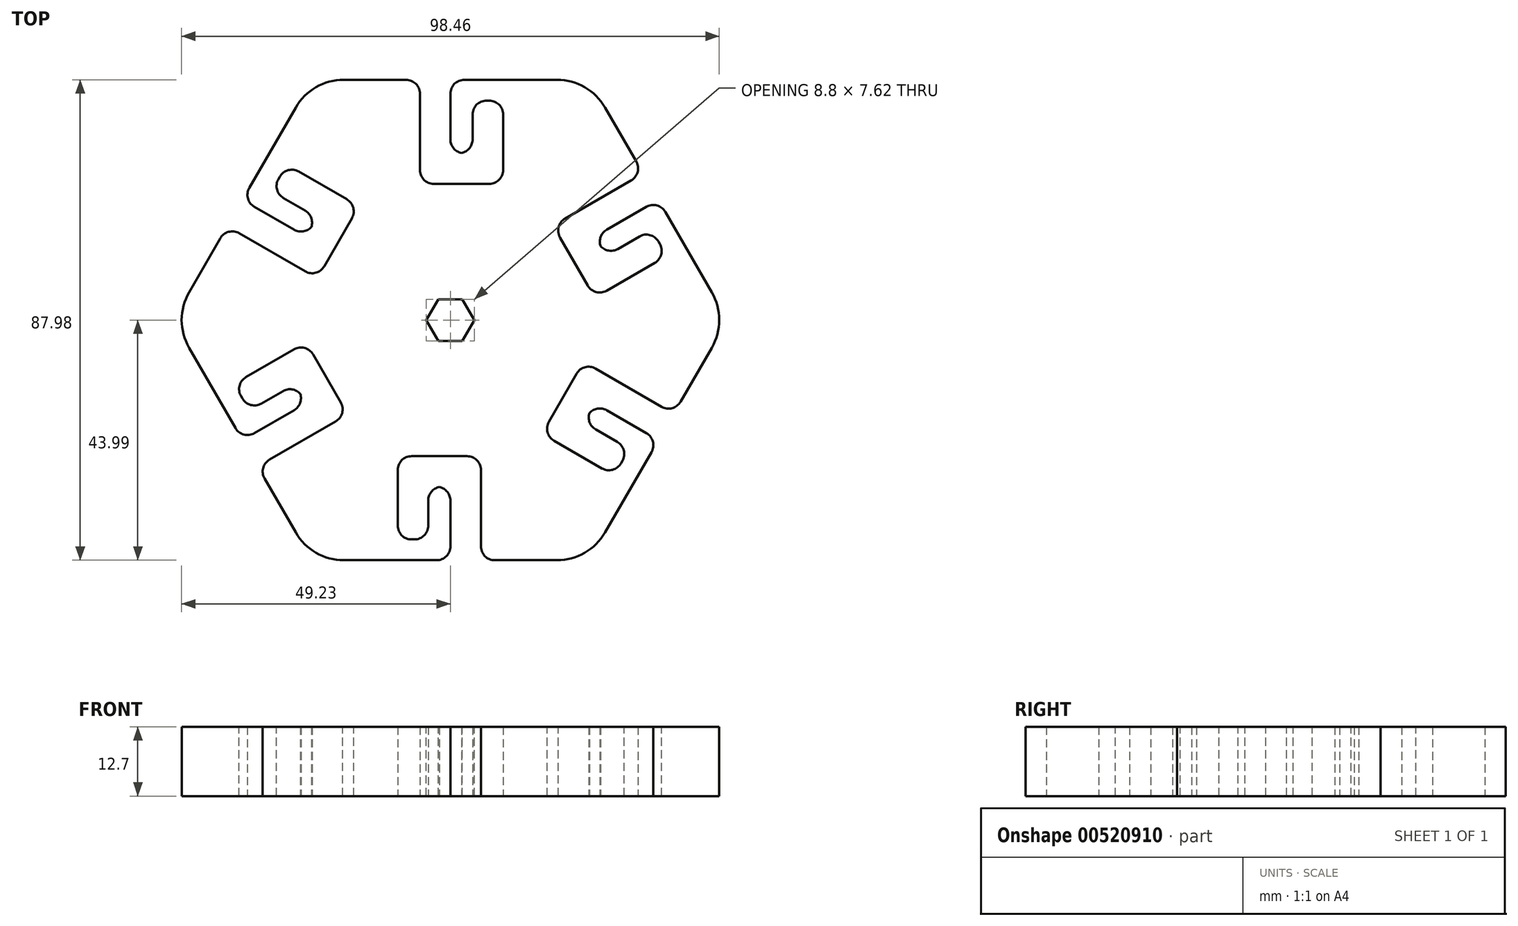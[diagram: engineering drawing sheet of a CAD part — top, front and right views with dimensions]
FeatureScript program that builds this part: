
annotation { "Feature Type Name" : "Feature", "Feature Type Description" : "" }
export const myFeature = defineFeature(function(context is Context, id is Id, definition is map)
    precondition{}
    {
        {
            var Q0;
            Q0=qCreatedBy(makeId("Top.planeOp"),FACE);
            var sketch = newSketch(context, id + "F0", { "sketchPlane" : qUnion([Q0])});
            skLineSegment(sketch, "E0", {"start": v(-5.59, 44) * mm, "end": v(-5.59, 24.94) * mm});
            skLineSegment(sketch, "E1", {"start": v(-5.59, 24.94) * mm, "end": v(9.65, 24.94) * mm});
            skLineSegment(sketch, "E2", {"start": v(9.65, 24.94) * mm, "end": v(9.65, 40.18) * mm});
            skLineSegment(sketch, "E3", {"start": v(9.65, 40.18) * mm, "end": v(4.06, 40.18) * mm});
            skLineSegment(sketch, "E4", {"start": v(4.06, 40.18) * mm, "end": v(4.06, 30.53) * mm});
            skLineSegment(sketch, "E5", {"start": v(4.06, 30.53) * mm, "end": v(0, 30.53) * mm});
            skLineSegment(sketch, "E6", {"start": v(0, 30.53) * mm, "end": v(0, 44) * mm});
            skCircle(sketch, "E7.cCircle", {"center": v(0, 0) * mm, "radius": 50.8 * mm, "construction": true});
            skLineSegment(sketch, "E7.0", {"start": v(25.4, -44) * mm, "end": v(-25.4, -44) * mm});
            skLineSegment(sketch, "E7.1", {"start": v(-25.4, -44) * mm, "end": v(-50.8, 0) * mm});
            skLineSegment(sketch, "E7.2", {"start": v(-50.8, 0) * mm, "end": v(-25.4, 44) * mm});
            skLineSegment(sketch, "E7.3", {"start": v(-25.4, 44) * mm, "end": v(25.4, 44) * mm});
            skLineSegment(sketch, "E7.4", {"start": v(25.4, 44) * mm, "end": v(50.8, 0) * mm});
            skLineSegment(sketch, "E7.5", {"start": v(50.8, 0) * mm, "end": v(25.4, -44) * mm});
            skLineSegment(sketch, "E8.1.0", {"start": v(-16.78, 20.83) * mm, "end": v(-29.97, 28.45) * mm});
            skLineSegment(sketch, "E8.1.1", {"start": v(-24.4, 7.63) * mm, "end": v(-16.78, 20.83) * mm});
            skLineSegment(sketch, "E8.1.2", {"start": v(-40.9, 17.16) * mm, "end": v(-24.4, 7.63) * mm});
            skLineSegment(sketch, "E8.1.3", {"start": v(-26.44, 15.27) * mm, "end": v(-38.1, 22) * mm});
            skLineSegment(sketch, "E8.1.4", {"start": v(-24.4, 18.79) * mm, "end": v(-26.44, 15.27) * mm});
            skLineSegment(sketch, "E8.1.5", {"start": v(-32.77, 23.61) * mm, "end": v(-24.4, 18.79) * mm});
            skLineSegment(sketch, "E8.1.6", {"start": v(-29.97, 28.45) * mm, "end": v(-32.77, 23.61) * mm});
            skLineSegment(sketch, "E8.2.0", {"start": v(-26.43, -4.11) * mm, "end": v(-39.63, -11.73) * mm});
            skLineSegment(sketch, "E8.2.1", {"start": v(-18.8, -17.31) * mm, "end": v(-26.43, -4.11) * mm});
            skLineSegment(sketch, "E8.2.2", {"start": v(-35.3, -26.84) * mm, "end": v(-18.8, -17.31) * mm});
            skLineSegment(sketch, "E8.2.3", {"start": v(-26.44, -15.27) * mm, "end": v(-38.1, -22) * mm});
            skLineSegment(sketch, "E8.2.4", {"start": v(-28.47, -11.75) * mm, "end": v(-26.44, -15.27) * mm});
            skLineSegment(sketch, "E8.2.5", {"start": v(-36.83, -16.57) * mm, "end": v(-28.47, -11.75) * mm});
            skLineSegment(sketch, "E8.2.6", {"start": v(-39.63, -11.73) * mm, "end": v(-36.83, -16.57) * mm});
            skLineSegment(sketch, "E8.3.0", {"start": v(-9.65, -24.94) * mm, "end": v(-9.65, -40.18) * mm});
            skLineSegment(sketch, "E8.3.1", {"start": v(5.59, -24.94) * mm, "end": v(-9.65, -24.94) * mm});
            skLineSegment(sketch, "E8.3.2", {"start": v(5.59, -44) * mm, "end": v(5.59, -24.94) * mm});
            skLineSegment(sketch, "E8.3.3", {"start": v(0, -30.53) * mm, "end": v(0, -44) * mm});
            skLineSegment(sketch, "E8.3.4", {"start": v(-4.06, -30.53) * mm, "end": v(0, -30.53) * mm});
            skLineSegment(sketch, "E8.3.5", {"start": v(-4.06, -40.18) * mm, "end": v(-4.06, -30.53) * mm});
            skLineSegment(sketch, "E8.3.6", {"start": v(-9.65, -40.18) * mm, "end": v(-4.06, -40.18) * mm});
            skLineSegment(sketch, "E8.4.0", {"start": v(16.78, -20.83) * mm, "end": v(29.97, -28.45) * mm});
            skLineSegment(sketch, "E8.4.1", {"start": v(24.4, -7.63) * mm, "end": v(16.78, -20.83) * mm});
            skLineSegment(sketch, "E8.4.2", {"start": v(40.9, -17.16) * mm, "end": v(24.4, -7.63) * mm});
            skLineSegment(sketch, "E8.4.3", {"start": v(26.44, -15.27) * mm, "end": v(38.1, -22) * mm});
            skLineSegment(sketch, "E8.4.4", {"start": v(24.4, -18.79) * mm, "end": v(26.44, -15.27) * mm});
            skLineSegment(sketch, "E8.4.5", {"start": v(32.77, -23.61) * mm, "end": v(24.4, -18.79) * mm});
            skLineSegment(sketch, "E8.4.6", {"start": v(29.97, -28.45) * mm, "end": v(32.77, -23.61) * mm});
            skLineSegment(sketch, "E8.5.0", {"start": v(26.43, 4.11) * mm, "end": v(39.63, 11.73) * mm});
            skLineSegment(sketch, "E8.5.1", {"start": v(18.8, 17.31) * mm, "end": v(26.43, 4.11) * mm});
            skLineSegment(sketch, "E8.5.2", {"start": v(35.3, 26.84) * mm, "end": v(18.8, 17.31) * mm});
            skLineSegment(sketch, "E8.5.3", {"start": v(26.44, 15.27) * mm, "end": v(38.1, 22) * mm});
            skLineSegment(sketch, "E8.5.4", {"start": v(28.47, 11.75) * mm, "end": v(26.44, 15.27) * mm});
            skLineSegment(sketch, "E8.5.5", {"start": v(36.83, 16.57) * mm, "end": v(28.47, 11.75) * mm});
            skLineSegment(sketch, "E8.5.6", {"start": v(39.63, 11.73) * mm, "end": v(36.83, 16.57) * mm});
            skPoint(sketch, "E9", {"position": v(2.03, 30.53) * mm});
            skSolve(sketch);
        }
        {
            var Q0;
            {var subQ12=sQuery(id+"F0.wireOp",EDGE,"E0");Q0=makeQuery(id+"F0.imprint","IMPRINT",FACE,{"disambiguationData":[TD([[makeQuery(id+"F0.imprint","IMPRINT",EDGE,{"derivedFrom":subQ12}),-1.0]])]});}
            extrude(context, id + "F1", {"entities" : qUnion([Q0]), "depth" : 12.7 * mm, "offsetDistance" : 25.4 * mm});
        }
        {
            var Q0;
            Q0=makeQuery(id+"F1.opExtrude","SWEPT_EDGE",EDGE,{"disambiguationData":[OSD([sQuery(id+"F0.wireOp",EDGE,"E7.1"),sQuery(id+"F0.wireOp",EDGE,"E7.2")])]});
            var Q1;
            Q1=makeQuery(id+"F1.opExtrude","SWEPT_EDGE",EDGE,{"disambiguationData":[OSD([sQuery(id+"F0.wireOp",EDGE,"E7.0"),sQuery(id+"F0.wireOp",EDGE,"E7.1")])]});
            var Q2;
            Q2=makeQuery(id+"F1.opExtrude","SWEPT_EDGE",EDGE,{"disambiguationData":[OSD([sQuery(id+"F0.wireOp",EDGE,"E7.0"),sQuery(id+"F0.wireOp",EDGE,"E7.5")])]});
            var Q3;
            Q3=makeQuery(id+"F1.opExtrude","SWEPT_EDGE",EDGE,{"disambiguationData":[OSD([sQuery(id+"F0.wireOp",EDGE,"E7.4"),sQuery(id+"F0.wireOp",EDGE,"E7.5")])]});
            var Q4;
            Q4=makeQuery(id+"F1.opExtrude","SWEPT_EDGE",EDGE,{"disambiguationData":[OSD([sQuery(id+"F0.wireOp",EDGE,"E7.3"),sQuery(id+"F0.wireOp",EDGE,"E7.4")])]});
            var Q5;
            Q5=makeQuery(id+"F1.opExtrude","SWEPT_EDGE",EDGE,{"disambiguationData":[OSD([sQuery(id+"F0.wireOp",EDGE,"E7.2"),sQuery(id+"F0.wireOp",EDGE,"E7.3")])]});
            fillet(context, id + "F2", {"entities" : qUnion([Q0, Q1, Q2, Q3, Q4, Q5]), "radius" : 10.16 * mm, "tangentPropagation" : true, "allowEdgeOverflow" : false});
        }
        {
            var Q0;
            Q0=makeQuery(id+"F1.opExtrude","SWEPT_EDGE",EDGE,{"disambiguationData":[OSD([sQuery(id+"F0.wireOp",EDGE,"E7.4"),sQuery(id+"F0.wireOp",EDGE,"E8.5.2")])]});
            var Q1;
            Q1=makeQuery(id+"F1.opExtrude","SWEPT_EDGE",EDGE,{"disambiguationData":[OSD([sQuery(id+"F0.wireOp",EDGE,"E8.5.1"),sQuery(id+"F0.wireOp",EDGE,"E8.5.2")])]});
            var Q2;
            Q2=makeQuery(id+"F1.opExtrude","SWEPT_EDGE",EDGE,{"disambiguationData":[OSD([sQuery(id+"F0.wireOp",EDGE,"E8.5.0"),sQuery(id+"F0.wireOp",EDGE,"E8.5.1")])]});
            var Q3;
            Q3=makeQuery(id+"F1.opExtrude","SWEPT_EDGE",EDGE,{"disambiguationData":[OSD([sQuery(id+"F0.wireOp",EDGE,"E8.5.0"),sQuery(id+"F0.wireOp",EDGE,"E8.5.6")])]});
            var Q4;
            Q4=makeQuery(id+"F1.opExtrude","SWEPT_EDGE",EDGE,{"disambiguationData":[OSD([sQuery(id+"F0.wireOp",EDGE,"E8.5.5"),sQuery(id+"F0.wireOp",EDGE,"E8.5.6")])]});
            var Q5;
            Q5=makeQuery(id+"F1.opExtrude","SWEPT_EDGE",EDGE,{"disambiguationData":[OSD([sQuery(id+"F0.wireOp",EDGE,"E8.5.4"),sQuery(id+"F0.wireOp",EDGE,"E8.5.5")])]});
            var Q6;
            Q6=makeQuery(id+"F1.opExtrude","SWEPT_EDGE",EDGE,{"disambiguationData":[OSD([sQuery(id+"F0.wireOp",EDGE,"E8.5.3"),sQuery(id+"F0.wireOp",EDGE,"E8.5.4")])]});
            var Q7;
            Q7=makeQuery(id+"F1.opExtrude","SWEPT_EDGE",EDGE,{"disambiguationData":[OSD([sQuery(id+"F0.wireOp",EDGE,"E7.4"),sQuery(id+"F0.wireOp",EDGE,"E8.5.3")])]});
            var Q8;
            Q8=makeQuery(id+"F1.opExtrude","SWEPT_EDGE",EDGE,{"disambiguationData":[OSD([sQuery(id+"F0.wireOp",EDGE,"E7.5"),sQuery(id+"F0.wireOp",EDGE,"E8.4.2")])]});
            var Q9;
            Q9=makeQuery(id+"F1.opExtrude","SWEPT_EDGE",EDGE,{"disambiguationData":[OSD([sQuery(id+"F0.wireOp",EDGE,"E7.5"),sQuery(id+"F0.wireOp",EDGE,"E8.4.3")])]});
            var Q10;
            Q10=makeQuery(id+"F1.opExtrude","SWEPT_EDGE",EDGE,{"disambiguationData":[OSD([sQuery(id+"F0.wireOp",EDGE,"E8.4.3"),sQuery(id+"F0.wireOp",EDGE,"E8.4.4")])]});
            var Q11;
            Q11=makeQuery(id+"F1.opExtrude","SWEPT_EDGE",EDGE,{"disambiguationData":[OSD([sQuery(id+"F0.wireOp",EDGE,"E8.4.1"),sQuery(id+"F0.wireOp",EDGE,"E8.4.2")])]});
            var Q12;
            Q12=makeQuery(id+"F1.opExtrude","SWEPT_EDGE",EDGE,{"disambiguationData":[OSD([sQuery(id+"F0.wireOp",EDGE,"E8.4.0"),sQuery(id+"F0.wireOp",EDGE,"E8.4.1")])]});
            var Q13;
            Q13=makeQuery(id+"F1.opExtrude","SWEPT_EDGE",EDGE,{"disambiguationData":[OSD([sQuery(id+"F0.wireOp",EDGE,"E8.4.0"),sQuery(id+"F0.wireOp",EDGE,"E8.4.6")])]});
            var Q14;
            Q14=makeQuery(id+"F1.opExtrude","SWEPT_EDGE",EDGE,{"disambiguationData":[OSD([sQuery(id+"F0.wireOp",EDGE,"E8.4.4"),sQuery(id+"F0.wireOp",EDGE,"E8.4.5")])]});
            var Q15;
            Q15=makeQuery(id+"F1.opExtrude","SWEPT_EDGE",EDGE,{"disambiguationData":[OSD([sQuery(id+"F0.wireOp",EDGE,"E8.4.5"),sQuery(id+"F0.wireOp",EDGE,"E8.4.6")])]});
            var Q16;
            Q16=makeQuery(id+"F1.opExtrude","SWEPT_EDGE",EDGE,{"disambiguationData":[OSD([sQuery(id+"F0.wireOp",EDGE,"E7.0"),sQuery(id+"F0.wireOp",EDGE,"E8.3.2")])]});
            var Q17;
            Q17=makeQuery(id+"F1.opExtrude","SWEPT_EDGE",EDGE,{"disambiguationData":[OSD([sQuery(id+"F0.wireOp",EDGE,"E7.0"),sQuery(id+"F0.wireOp",EDGE,"E8.3.3")])]});
            var Q18;
            Q18=makeQuery(id+"F1.opExtrude","SWEPT_EDGE",EDGE,{"disambiguationData":[OSD([sQuery(id+"F0.wireOp",EDGE,"E8.3.1"),sQuery(id+"F0.wireOp",EDGE,"E8.3.2")])]});
            var Q19;
            Q19=makeQuery(id+"F1.opExtrude","SWEPT_EDGE",EDGE,{"disambiguationData":[OSD([sQuery(id+"F0.wireOp",EDGE,"E8.3.0"),sQuery(id+"F0.wireOp",EDGE,"E8.3.1")])]});
            var Q20;
            Q20=makeQuery(id+"F1.opExtrude","SWEPT_EDGE",EDGE,{"disambiguationData":[OSD([sQuery(id+"F0.wireOp",EDGE,"E8.3.0"),sQuery(id+"F0.wireOp",EDGE,"E8.3.6")])]});
            var Q21;
            Q21=makeQuery(id+"F1.opExtrude","SWEPT_EDGE",EDGE,{"disambiguationData":[OSD([sQuery(id+"F0.wireOp",EDGE,"E8.3.5"),sQuery(id+"F0.wireOp",EDGE,"E8.3.6")])]});
            var Q22;
            Q22=makeQuery(id+"F1.opExtrude","SWEPT_EDGE",EDGE,{"disambiguationData":[OSD([sQuery(id+"F0.wireOp",EDGE,"E8.3.4"),sQuery(id+"F0.wireOp",EDGE,"E8.3.5")])]});
            var Q23;
            Q23=makeQuery(id+"F1.opExtrude","SWEPT_EDGE",EDGE,{"disambiguationData":[OSD([sQuery(id+"F0.wireOp",EDGE,"E8.3.3"),sQuery(id+"F0.wireOp",EDGE,"E8.3.4")])]});
            var Q24;
            Q24=makeQuery(id+"F1.opExtrude","SWEPT_EDGE",EDGE,{"disambiguationData":[OSD([sQuery(id+"F0.wireOp",EDGE,"E7.1"),sQuery(id+"F0.wireOp",EDGE,"E8.2.2")])]});
            var Q25;
            Q25=makeQuery(id+"F1.opExtrude","SWEPT_EDGE",EDGE,{"disambiguationData":[OSD([sQuery(id+"F0.wireOp",EDGE,"E8.2.1"),sQuery(id+"F0.wireOp",EDGE,"E8.2.2")])]});
            var Q26;
            Q26=makeQuery(id+"F1.opExtrude","SWEPT_EDGE",EDGE,{"disambiguationData":[OSD([sQuery(id+"F0.wireOp",EDGE,"E8.2.0"),sQuery(id+"F0.wireOp",EDGE,"E8.2.1")])]});
            var Q27;
            Q27=makeQuery(id+"F1.opExtrude","SWEPT_EDGE",EDGE,{"disambiguationData":[OSD([sQuery(id+"F0.wireOp",EDGE,"E8.2.0"),sQuery(id+"F0.wireOp",EDGE,"E8.2.6")])]});
            var Q28;
            Q28=makeQuery(id+"F1.opExtrude","SWEPT_EDGE",EDGE,{"disambiguationData":[OSD([sQuery(id+"F0.wireOp",EDGE,"E8.2.4"),sQuery(id+"F0.wireOp",EDGE,"E8.2.5")])]});
            var Q29;
            Q29=makeQuery(id+"F1.opExtrude","SWEPT_EDGE",EDGE,{"disambiguationData":[OSD([sQuery(id+"F0.wireOp",EDGE,"E8.2.5"),sQuery(id+"F0.wireOp",EDGE,"E8.2.6")])]});
            var Q30;
            Q30=makeQuery(id+"F1.opExtrude","SWEPT_EDGE",EDGE,{"disambiguationData":[OSD([sQuery(id+"F0.wireOp",EDGE,"E8.2.3"),sQuery(id+"F0.wireOp",EDGE,"E8.2.4")])]});
            var Q31;
            Q31=makeQuery(id+"F1.opExtrude","SWEPT_EDGE",EDGE,{"disambiguationData":[OSD([sQuery(id+"F0.wireOp",EDGE,"E7.1"),sQuery(id+"F0.wireOp",EDGE,"E8.2.3")])]});
            var Q32;
            Q32=makeQuery(id+"F1.opExtrude","SWEPT_EDGE",EDGE,{"disambiguationData":[OSD([sQuery(id+"F0.wireOp",EDGE,"E7.2"),sQuery(id+"F0.wireOp",EDGE,"E8.1.2")])]});
            var Q33;
            Q33=makeQuery(id+"F1.opExtrude","SWEPT_EDGE",EDGE,{"disambiguationData":[OSD([sQuery(id+"F0.wireOp",EDGE,"E7.2"),sQuery(id+"F0.wireOp",EDGE,"E8.1.3")])]});
            var Q34;
            Q34=makeQuery(id+"F1.opExtrude","SWEPT_EDGE",EDGE,{"disambiguationData":[OSD([sQuery(id+"F0.wireOp",EDGE,"E8.1.3"),sQuery(id+"F0.wireOp",EDGE,"E8.1.4")])]});
            var Q35;
            Q35=makeQuery(id+"F1.opExtrude","SWEPT_EDGE",EDGE,{"disambiguationData":[OSD([sQuery(id+"F0.wireOp",EDGE,"E8.1.4"),sQuery(id+"F0.wireOp",EDGE,"E8.1.5")])]});
            var Q36;
            Q36=makeQuery(id+"F1.opExtrude","SWEPT_EDGE",EDGE,{"disambiguationData":[OSD([sQuery(id+"F0.wireOp",EDGE,"E8.1.5"),sQuery(id+"F0.wireOp",EDGE,"E8.1.6")])]});
            var Q37;
            Q37=makeQuery(id+"F1.opExtrude","SWEPT_EDGE",EDGE,{"disambiguationData":[OSD([sQuery(id+"F0.wireOp",EDGE,"E8.1.1"),sQuery(id+"F0.wireOp",EDGE,"E8.1.2")])]});
            var Q38;
            Q38=makeQuery(id+"F1.opExtrude","SWEPT_EDGE",EDGE,{"disambiguationData":[OSD([sQuery(id+"F0.wireOp",EDGE,"E8.1.0"),sQuery(id+"F0.wireOp",EDGE,"E8.1.1")])]});
            var Q39;
            Q39=makeQuery(id+"F1.opExtrude","SWEPT_EDGE",EDGE,{"disambiguationData":[OSD([sQuery(id+"F0.wireOp",EDGE,"E8.1.0"),sQuery(id+"F0.wireOp",EDGE,"E8.1.6")])]});
            var Q40;
            Q40=makeQuery(id+"F1.opExtrude","SWEPT_EDGE",EDGE,{"disambiguationData":[OSD([sQuery(id+"F0.wireOp",EDGE,"E0"),sQuery(id+"F0.wireOp",EDGE,"E7.3")])]});
            var Q41;
            Q41=makeQuery(id+"F1.opExtrude","SWEPT_EDGE",EDGE,{"disambiguationData":[OSD([sQuery(id+"F0.wireOp",EDGE,"E0"),sQuery(id+"F0.wireOp",EDGE,"E1")])]});
            var Q42;
            Q42=makeQuery(id+"F1.opExtrude","SWEPT_EDGE",EDGE,{"disambiguationData":[OSD([sQuery(id+"F0.wireOp",EDGE,"E6"),sQuery(id+"F0.wireOp",EDGE,"E7.3")])]});
            var Q43;
            Q43=makeQuery(id+"F1.opExtrude","SWEPT_EDGE",EDGE,{"disambiguationData":[OSD([sQuery(id+"F0.wireOp",EDGE,"E5"),sQuery(id+"F0.wireOp",EDGE,"E6")])]});
            var Q44;
            Q44=makeQuery(id+"F1.opExtrude","SWEPT_EDGE",EDGE,{"disambiguationData":[OSD([sQuery(id+"F0.wireOp",EDGE,"E3"),sQuery(id+"F0.wireOp",EDGE,"E4")])]});
            var Q45;
            Q45=makeQuery(id+"F1.opExtrude","SWEPT_EDGE",EDGE,{"disambiguationData":[OSD([sQuery(id+"F0.wireOp",EDGE,"E4"),sQuery(id+"F0.wireOp",EDGE,"E5")])]});
            var Q46;
            Q46=makeQuery(id+"F1.opExtrude","SWEPT_EDGE",EDGE,{"disambiguationData":[OSD([sQuery(id+"F0.wireOp",EDGE,"E1"),sQuery(id+"F0.wireOp",EDGE,"E2")])]});
            var Q47;
            Q47=makeQuery(id+"F1.opExtrude","SWEPT_EDGE",EDGE,{"disambiguationData":[OSD([sQuery(id+"F0.wireOp",EDGE,"E2"),sQuery(id+"F0.wireOp",EDGE,"E3")])]});
            fillet(context, id + "F3", {"entities" : qUnion([Q0, Q1, Q2, Q3, Q4, Q5, Q6, Q7, Q8, Q9, Q10, Q11, Q12, Q13, Q14, Q15, Q16, Q17, Q18, Q19, Q20, Q21, Q22, Q23, Q24, Q25, Q26, Q27, Q28, Q29, Q30, Q31, Q32, Q33, Q34, Q35, Q36, Q37, Q38, Q39, Q40, Q41, Q42, Q43, Q44, Q45, Q46, Q47]), "radius" : 2.54 * mm, "tangentPropagation" : true, "allowEdgeOverflow" : false});
        }
        {
            var Q0;
            Q0=makeQuery(id+"F1.opExtrude","CAP_FACE",FACE,{"disambiguationData":[OSD([sQuery(id+"F0.wireOp",EDGE,"E0"),sQuery(id+"F0.wireOp",EDGE,"E1"),sQuery(id+"F0.wireOp",EDGE,"E2"),sQuery(id+"F0.wireOp",EDGE,"E3"),sQuery(id+"F0.wireOp",EDGE,"E4"),sQuery(id+"F0.wireOp",EDGE,"E5"),sQuery(id+"F0.wireOp",EDGE,"E6"),sQuery(id+"F0.wireOp",EDGE,"E7.0"),sQuery(id+"F0.wireOp",EDGE,"E7.1"),sQuery(id+"F0.wireOp",EDGE,"E7.2"),sQuery(id+"F0.wireOp",EDGE,"E7.3"),sQuery(id+"F0.wireOp",EDGE,"E7.4"),sQuery(id+"F0.wireOp",EDGE,"E7.5"),sQuery(id+"F0.wireOp",EDGE,"E8.1.0"),sQuery(id+"F0.wireOp",EDGE,"E8.1.1"),sQuery(id+"F0.wireOp",EDGE,"E8.1.2"),sQuery(id+"F0.wireOp",EDGE,"E8.1.3"),sQuery(id+"F0.wireOp",EDGE,"E8.1.4"),sQuery(id+"F0.wireOp",EDGE,"E8.1.5"),sQuery(id+"F0.wireOp",EDGE,"E8.1.6"),sQuery(id+"F0.wireOp",EDGE,"E8.2.0"),sQuery(id+"F0.wireOp",EDGE,"E8.2.1"),sQuery(id+"F0.wireOp",EDGE,"E8.2.2"),sQuery(id+"F0.wireOp",EDGE,"E8.2.3"),sQuery(id+"F0.wireOp",EDGE,"E8.2.4"),sQuery(id+"F0.wireOp",EDGE,"E8.2.5"),sQuery(id+"F0.wireOp",EDGE,"E8.2.6"),sQuery(id+"F0.wireOp",EDGE,"E8.3.0"),sQuery(id+"F0.wireOp",EDGE,"E8.3.1"),sQuery(id+"F0.wireOp",EDGE,"E8.3.2"),sQuery(id+"F0.wireOp",EDGE,"E8.3.3"),sQuery(id+"F0.wireOp",EDGE,"E8.3.4"),sQuery(id+"F0.wireOp",EDGE,"E8.3.5"),sQuery(id+"F0.wireOp",EDGE,"E8.3.6"),sQuery(id+"F0.wireOp",EDGE,"E8.4.0"),sQuery(id+"F0.wireOp",EDGE,"E8.4.1"),sQuery(id+"F0.wireOp",EDGE,"E8.4.2"),sQuery(id+"F0.wireOp",EDGE,"E8.4.3"),sQuery(id+"F0.wireOp",EDGE,"E8.4.4"),sQuery(id+"F0.wireOp",EDGE,"E8.4.5"),sQuery(id+"F0.wireOp",EDGE,"E8.4.6"),sQuery(id+"F0.wireOp",EDGE,"E8.5.0"),sQuery(id+"F0.wireOp",EDGE,"E8.5.1"),sQuery(id+"F0.wireOp",EDGE,"E8.5.2"),sQuery(id+"F0.wireOp",EDGE,"E8.5.3"),sQuery(id+"F0.wireOp",EDGE,"E8.5.4"),sQuery(id+"F0.wireOp",EDGE,"E8.5.5"),sQuery(id+"F0.wireOp",EDGE,"E8.5.6")])],"isStart":false});
            var sketch = newSketch(context, id + "F4", { "sketchPlane" : qUnion([Q0])});
            skCircle(sketch, "E10.cCircle", {"center": v(0, 0) * mm, "radius": 3.81 * mm, "construction": true});
            skLineSegment(sketch, "E10.0", {"start": v(4.4, 0) * mm, "end": v(2.2, -3.8) * mm});
            skLineSegment(sketch, "E10.1", {"start": v(2.2, -3.81) * mm, "end": v(-2.2, -3.81) * mm});
            skLineSegment(sketch, "E10.2", {"start": v(-2.2, -3.8) * mm, "end": v(-4.4, 0) * mm});
            skLineSegment(sketch, "E10.3", {"start": v(-4.4, 0) * mm, "end": v(-2.2, 3.81) * mm});
            skLineSegment(sketch, "E10.4", {"start": v(-2.2, 3.81) * mm, "end": v(2.2, 3.81) * mm});
            skLineSegment(sketch, "E10.5", {"start": v(2.2, 3.81) * mm, "end": v(4.4, 0) * mm});
            skPoint(sketch, "E10.0.midPoint", {"position": v(3.3, -1.9) * mm});
            skSolve(sketch);
        }
        {
            var Q0;
            Q0=makeQuery(id+"F4.imprint","IMPRINT",FACE,{"disambiguationData":[TD([[makeQuery(id+"F4.imprint","IMPRINT",EDGE,{"derivedFrom":sQuery(id+"F4.wireOp",EDGE,"E10.0")}),-1.0]])]});
            extrude(context, id + "F5", {"entities" : qUnion([Q0]), "operationType" : NewBodyOperationType.REMOVE, "endBound" : BoundingType.THROUGH_ALL, "oppositeDirection" : true, "depth" : 25.4 * mm, "offsetDistance" : 25.4 * mm});
        }
    });
